# Revit family: HEATER
name_source: partatom
category: Wyposażenie mechaniczne
revit_build: Autodesk Revit 2018 (Build: 20170927_1515(x64)
units: mm (PartAtom-declared; Revit-internal decimal feet)

## family parameters
Klasyfikacja = Brak
Obiekt nadrzędny = Powierzchnia
Punkt obliczania pomieszczeń = Nie
Tnij formami wycięć po wczytaniu = Nie
Typ części = Normalny
Współdzielony = Nie
Wymiar okrągłego złącza = Użyj średnicy

## types (8) — shared parameters
Autor = www.archispace.com
Domyślna rzędna = 1219 mm
Opis = Nagrzewnica wodna
Producent = SONNIGER Polska Sp. z o.o. Sp. k.
klasa IP = IP54
maksymalna temp. czynnika = 120 °C
maksymalne ciśnienie robocze = 1600000.0 Pa
materiał = 230,230,230
napięcie zasilania = 230 V
zero-valued in all types: głośność pracy (dB)

## per-type parameters (varying)
| type | Maksymalny zasięg powietrza | Moc grzewcza max. | Moc grzewcza min. | Model | O | PPU | ilość rzędów nagrzewnicy | maksymalny wydatek powietrza | moc silnika elektrycznego | obroty silnika (obr/min) | poziom głośności pracy | waga bez wody | waga z wodą | ΔT |
| CR ONE - montaż naścienny | 14000 mm | 20 kW | 7 kW | Heater CONDENS CR ONE | 0 mm | PPU : HORIZONTAL - ONE, R1 | 2 | 1600.0 m³/h | 124 W | 1400 | I bieg 35 dB / II bieg 46 dB / III bieg 52 dB | 9.60 kg | 10.70 kg | 25 °C |
| CR1 - montaż naścienny | 27000 mm | 30 kW | 9 kW | Heater CONDENS CR1 | 0 mm | PPU : HORIZONTAL - ONE, R1 | 1 | 3900.0 m³/h | 250 W | 1350 | I bieg 44 dB / II bieg 52 dB / III bieg 62 dB | 10.80 kg | 11.90 kg | 13 °C |
| CR2 - montaż naścienny | 25000 mm | 50 kW | 13 kW | Heater CONDENS CR2 | 0 mm | PPU : HORIZONTAL - R2, SPECIAL | 2 | 3350.0 m³/h | 250 W | 1350 | I bieg 41 dB / II bieg 50 dB / III bieg 60 dB | 12.70 kg | 14.80 kg | 22 °C |
| CR3 - montaż naścienny | 24000 mm | 70 kW | 20 kW | Heater CONDENS CR3 | 0 mm | PPU : HORIZONTAL - R3 | 3 | 2950.0 m³/h | 250 W | 1350 | I bieg 39 dB / II bieg 48 dB / III bieg 58 dB | 14.50 kg | 16.90 kg | 34 °C |
| CR ONE - montaż na suficie | 14000 mm | 20 kW | 7 kW | Heater CONDENS CR ONE | 201 mm | PPU : VERTICAL - ONE | 2 | 1600.0 m³/h | 124 W | 1400 | I bieg 35 dB / II bieg 46 dB / III bieg 52 dB | 9.60 kg | 10.70 kg | 25 °C |
| CR1 - montaż na suficie | 27000 mm | 30 kW | 9 kW | Heater CONDENS CR1 | 227 mm | PPU : VERTICAL - R1, R2, R3, SPECIAL | 1 | 3900.0 m³/h | 250 W | 1350 | I bieg 44 dB / II bieg 52 dB / III bieg 62 dB | 10.80 kg | 11.90 kg | 13 °C |
| CR2 - montaż na suficie | 25000 mm | 50 kW | 13 kW | Heater CONDENS CR2 | 227 mm | PPU : VERTICAL - R1, R2, R3, SPECIAL | 2 | 3350.0 m³/h | 250 W | 1350 | I bieg 41 dB / II bieg 50 dB / III bieg 60 dB | 12.70 kg | 14.80 kg | 22 °C |
| CR3 - montaż na suficie | 24000 mm | 70 kW | 20 kW | Heater CONDENS CR3 | 227 mm | PPU : VERTICAL - R1, R2, R3, SPECIAL | 3 | 2950.0 m³/h | 250 W | 1350 | I bieg 39 dB / II bieg 48 dB / III bieg 58 dB | 14.50 kg | 16.90 kg | 34 °C |
